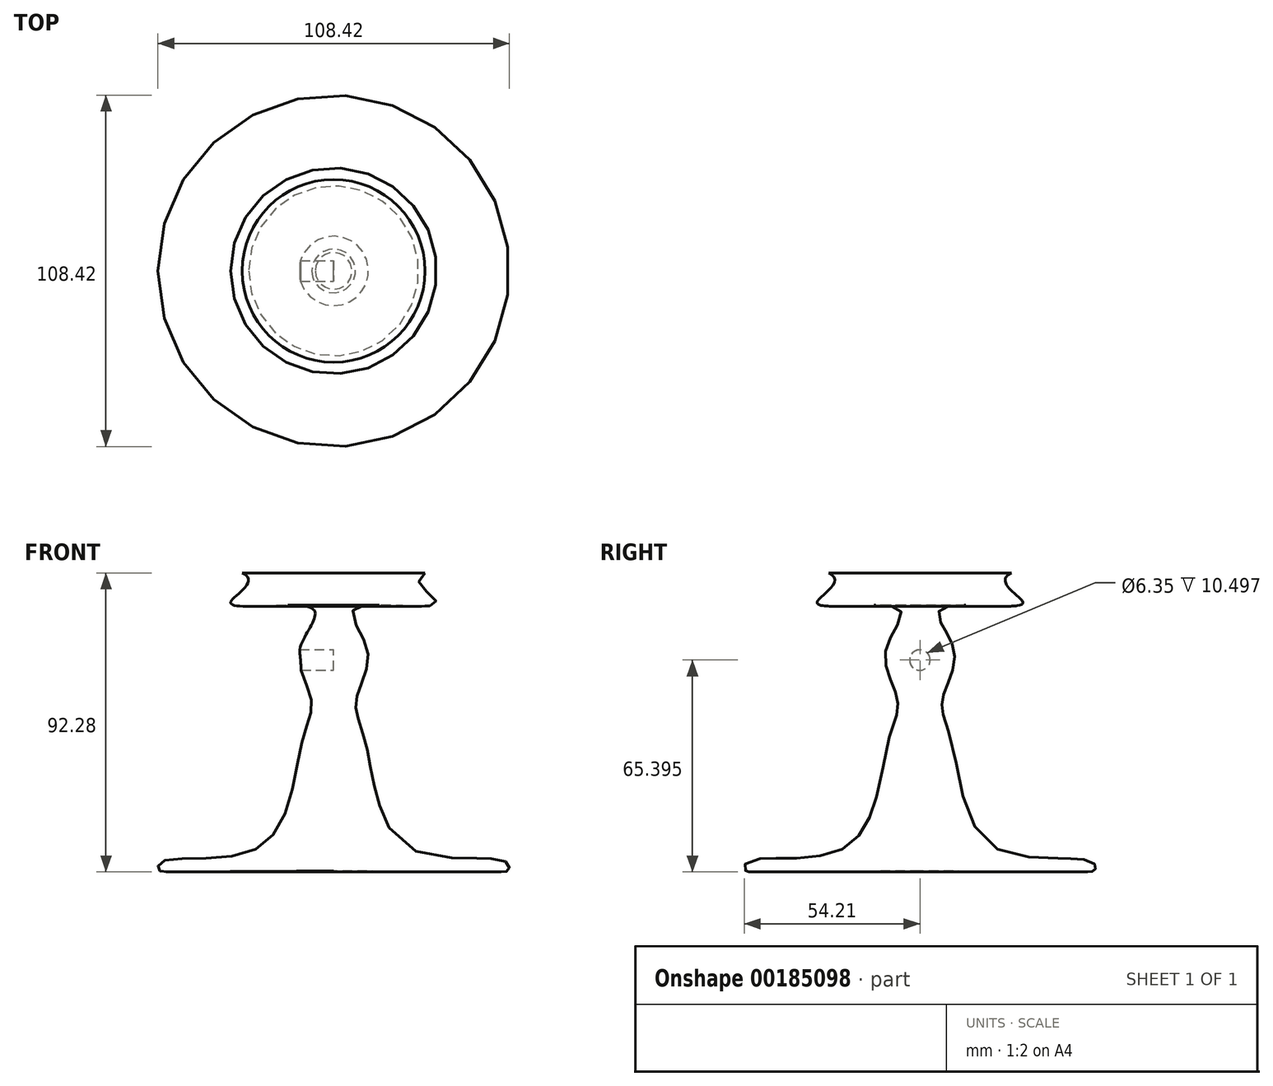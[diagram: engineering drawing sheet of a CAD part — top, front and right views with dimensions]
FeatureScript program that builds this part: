
annotation { "Feature Type Name" : "Feature", "Feature Type Description" : "" }
export const myFeature = defineFeature(function(context is Context, id is Id, definition is map)
    precondition{}
    {
        {
            var Q0;
            Q0=qCreatedBy(makeId("Front.planeOp"),FACE);
            var sketch = newSketch(context, id + "F0", { "sketchPlane" : qUnion([Q0])});
            skFitSpline(sketch, "E0", {"points": [v(-28.2, 44.68) * mm, v(-31.75, 35.65) * mm, v(-6.59, 33.71) * mm, v(-10.46, 21.13) * mm, v(-6.91, 5.65) * mm, v(-9.81, -7.58) * mm, v(-22.72, -39.84) * mm, v(-53.04, -44.36) * mm, v(-54.01, -46.94) * mm, v(-50.46, -47.58) * mm, v(0, -47.26) * mm], "startDerivative": vector(232.72, -105.32) * mm, "endDerivative": vector(399.01, 3.62) * mm});
            skLineSegment(sketch, "E1", {"start": v(-28.2, 44.68) * mm, "end": v(0, 44.68) * mm});
            skLineSegment(sketch, "E2", {"start": v(0, 44.68) * mm, "end": v(0, -47.26) * mm});
            skSolve(sketch);
        }
        {
            var Q0;
            Q0=makeQuery(id+"F0.imprint","IMPRINT",FACE,{"disambiguationData":[TD([[makeQuery(id+"F0.imprint","IMPRINT",EDGE,{"derivedFrom":sQuery(id+"F0.wireOp",EDGE,"E0")}),1.0]])]});
            var Q1;
            Q1=sQuery(id+"F0.wireOp",EDGE,"E2");
            revolve(context, id + "F1", {"entities" : qUnion([Q0]), "axis" : qUnion([Q1]), "revolveType" : RevolveType.FULL});
        }
        {
            var Q0;
            Q0=qCreatedBy(makeId("Right.planeOp"),FACE);
            var sketch = newSketch(context, id + "F2", { "sketchPlane" : qUnion([Q0])});
            skCircle(sketch, "E3", {"center": v(0, 17.8) * mm, "radius": 6.82 * mm});
            skSolve(sketch);
        }
        {
            var Q0;
            Q0=sQuery(id+"F2.wireOp",VERTEX,"E3.center");
            var Q1;
            Q1=makeQuery(id+"F1.opRevolve","SWEPT_BODY",BODY,{"disambiguationData":[OSD([sQuery(id+"F0.wireOp",EDGE,"E0"),sQuery(id+"F0.wireOp",EDGE,"E1"),sQuery(id+"F0.wireOp",EDGE,"E2")])]});
            hole(context, id + "F3", {"style" : HoleStyle.SIMPLE, "endStyle" : HoleEndStyle.THROUGH, "holeDiameter" : 6.35 * mm, "locations" : qUnion([Q0]), "scope" : qUnion([Q1]), "isTappedThrough" : true});
        }
    });
